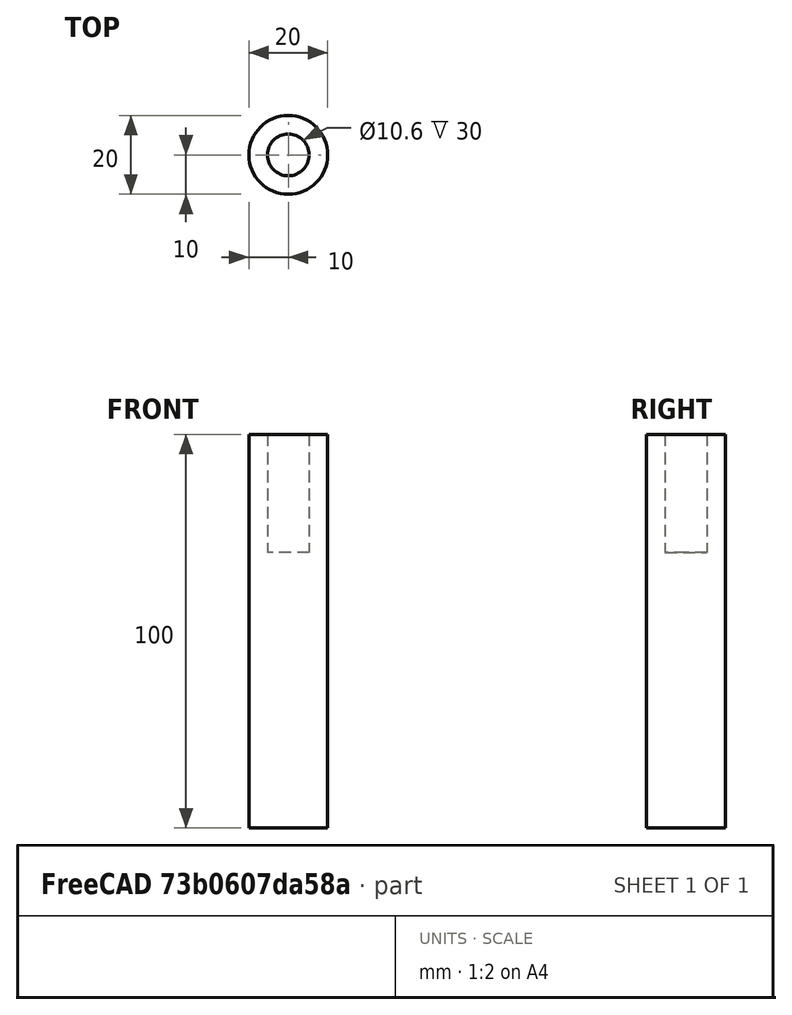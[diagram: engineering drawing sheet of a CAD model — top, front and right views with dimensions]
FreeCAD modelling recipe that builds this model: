
FCSTD DOCUMENT  (FreeCAD 0.17R12794 (Git))
Label: pillar
License: All rights reserved
LicenseURL: http://en.wikipedia.org/wiki/All_rights_reserved
objects: Sketcher::SketchObject×1, PartDesign::Revolution×1
note: 3 computed .brp shape members not serialized (recipe doc carries the construction recipe); baked Part::Feature solids carry a one-line shape summary decoded from their .brp

FEATURE [Sketcher::SketchObject] Sketch
  MapMode = 5
  Placement = pos=(0,0,0) rot=(1,0,0;1.5708rad)
  sketch-geometry (6):
    g0: LineSegment StartX=0 StartY=70 StartZ=0 EndX=0 EndY=0 EndZ=0
    g1: LineSegment StartX=0 StartY=0 StartZ=0 EndX=10 EndY=0 EndZ=0
    g2: LineSegment StartX=10 StartY=0 StartZ=0 EndX=10 EndY=100 EndZ=0
    g3: LineSegment StartX=10 StartY=100 StartZ=0 EndX=5.3 EndY=100 EndZ=0
    g4: LineSegment StartX=5.3 StartY=100 StartZ=0 EndX=5.3 EndY=70 EndZ=0
    g5: LineSegment StartX=5.3 StartY=70 StartZ=0 EndX=0 EndY=70 EndZ=0
  constraints (17):
    c: Coincident(g0,g-1)
    c: Vertical(g0)
    c: Coincident(g0,g1)
    c: Horizontal(g1)
    c: Coincident(g1,g2)
    c: Vertical(g2)
    c: Coincident(g2,g3)
    c: Coincident(g3,g4)
    c: Vertical(g4)
    c: Coincident(g4,g5)
    c: Coincident(g5,g0)
    c: Parallel(g5,g1)
    c: Parallel(g3,g1)
    c: DistanceY(g2,g2) = 100
    c: DistanceX(g1,g1) = 10
    c: DistanceY(g4,g4) = 30
    c: DistanceX(g5,g5) = 5.3
FEATURE [PartDesign::Revolution] Revolution  label="pillar"
  Angle = 360
  Axis = (0,0,1)
  Base = (0,0,0)
  Placement = pos=(0,0,0) rot=(1,0,0;1.5708rad)
  Profile = -> Sketch
  ReferenceAxis = -> Sketch [V_Axis]
  Reversed = true
